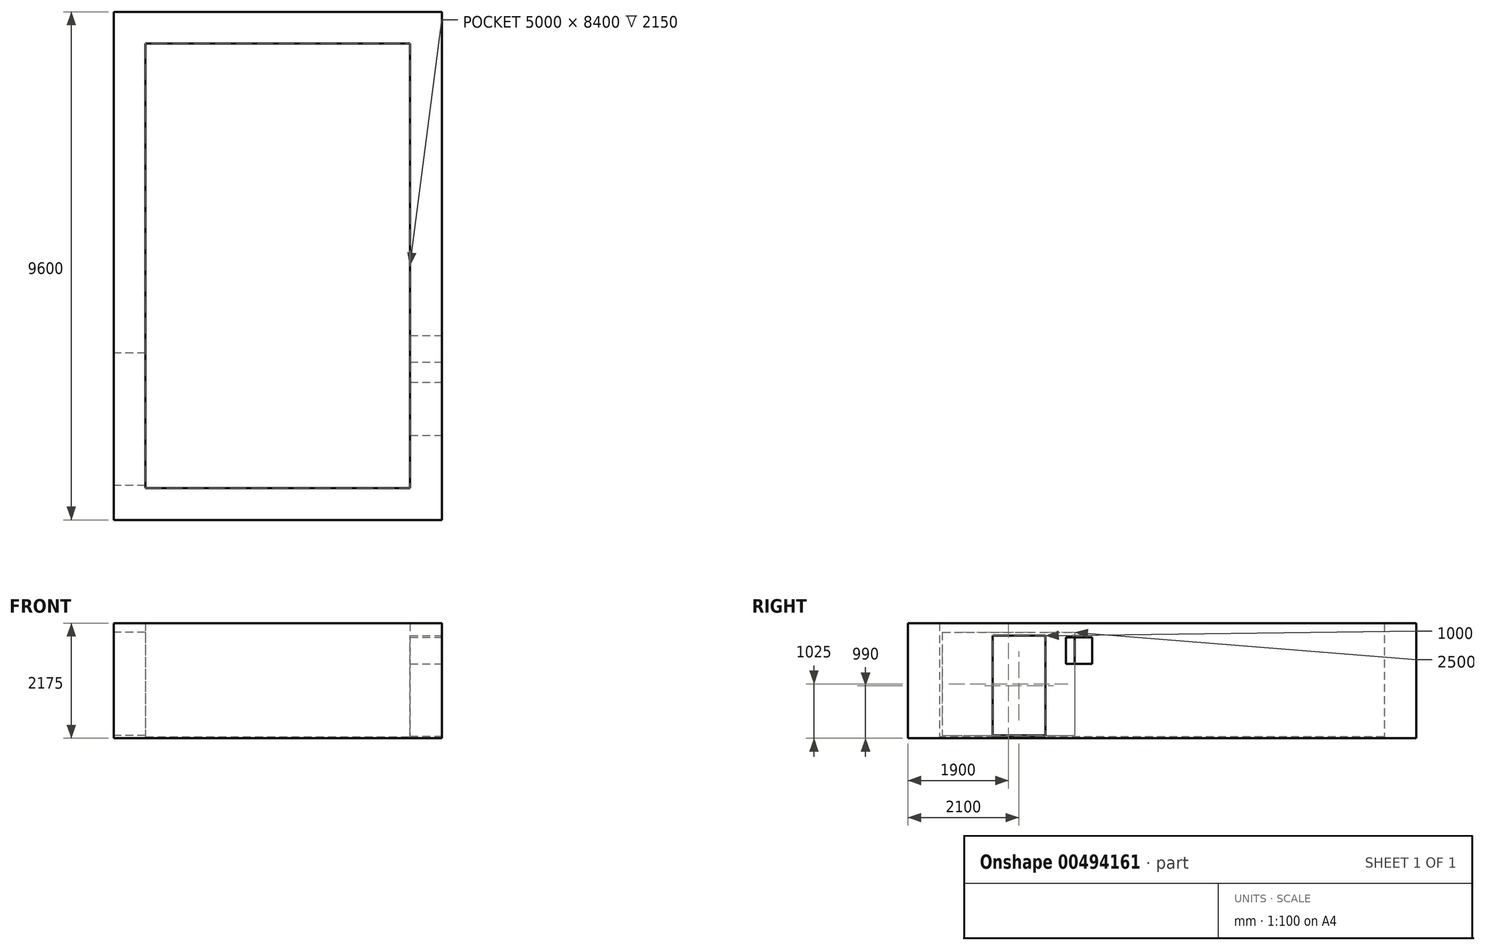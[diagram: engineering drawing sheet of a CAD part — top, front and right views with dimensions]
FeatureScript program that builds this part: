
annotation { "Feature Type Name" : "Feature", "Feature Type Description" : "" }
export const myFeature = defineFeature(function(context is Context, id is Id, definition is map)
    precondition{}
    {
        {
            var Q0;
            Q0=qCreatedBy(makeId("Top.planeOp"),FACE);
            var sketch = newSketch(context, id + "F0", { "sketchPlane" : qUnion([Q0])});
            skLineSegment(sketch, "E0.bottom", {"start": v(-2500, 4200) * mm, "end": v(2500, 4200) * mm});
            skLineSegment(sketch, "E0.top", {"start": v(-2500, -4200) * mm, "end": v(2500, -4200) * mm});
            skLineSegment(sketch, "E0.left", {"start": v(-2500, 4200) * mm, "end": v(-2500, -4200) * mm});
            skLineSegment(sketch, "E0.right", {"start": v(2500, 4200) * mm, "end": v(2500, -4200) * mm});
            skLineSegment(sketch, "E1", {"start": v(-2500, -4200) * mm, "end": v(2500, 4200) * mm, "construction": true});
            skLineSegment(sketch, "E2.0", {"start": v(3100, 4800) * mm, "end": v(3100, -4800) * mm});
            skLineSegment(sketch, "E2.1", {"start": v(-3100, 4800) * mm, "end": v(3100, 4800) * mm});
            skLineSegment(sketch, "E2.2", {"start": v(-3100, 4800) * mm, "end": v(-3100, -4800) * mm});
            skLineSegment(sketch, "E2.3", {"start": v(-3100, -4800) * mm, "end": v(3100, -4800) * mm});
            skSolve(sketch);
        }
        {
            var Q0;
            Q0 = qSketchRegion(id + "F0", true);
            extrude(context, id + "F1", {"entities" : qUnion([Q0]), "depth" : 2150 * mm, "offsetDistance" : 25 * mm});
        }
        {
            var Q0;
            Q0=makeQuery(id+"F1.opExtrude","CAP_FACE",FACE,{"disambiguationData":[OSD([sQuery(id+"F0.wireOp",EDGE,"E0.bottom"),sQuery(id+"F0.wireOp",EDGE,"E0.top"),sQuery(id+"F0.wireOp",EDGE,"E0.left"),sQuery(id+"F0.wireOp",EDGE,"E0.right"),sQuery(id+"F0.wireOp",EDGE,"E2.0"),sQuery(id+"F0.wireOp",EDGE,"E2.1"),sQuery(id+"F0.wireOp",EDGE,"E2.2"),sQuery(id+"F0.wireOp",EDGE,"E2.3")])],"isStart":true});
            var sketch = newSketch(context, id + "F2", { "sketchPlane" : qUnion([Q0])});
            skLineSegment(sketch, "E3.bottom", {"start": v(-3100, 4800) * mm, "end": v(3100, 4800) * mm});
            skLineSegment(sketch, "E3.top", {"start": v(-3100, -4800) * mm, "end": v(3100, -4800) * mm});
            skLineSegment(sketch, "E3.left", {"start": v(-3100, 4800) * mm, "end": v(-3100, -4800) * mm});
            skLineSegment(sketch, "E3.right", {"start": v(3100, 4800) * mm, "end": v(3100, -4800) * mm});
            skSolve(sketch);
        }
        {
            var Q0;
            Q0 = qSketchRegion(id + "F2", true);
            extrude(context, id + "F3", {"entities" : qUnion([Q0]), "operationType" : NewBodyOperationType.ADD, "depth" : 25 * mm, "offsetDistance" : 25 * mm});
        }
        {
            var Q0;
            Q0=makeQuery(id+"F3.boolean.opBoolean","MERGE",FACE,{"derivedFrom":[makeQuery(id+"F1.opExtrude","SWEPT_FACE",FACE,{"disambiguationData":[OSD([sQuery(id+"F0.wireOp",EDGE,"E2.2")])]}),makeQuery(id+"F3.opExtrude","SWEPT_FACE",FACE,{"disambiguationData":[OSD([sQuery(id+"F2.wireOp",EDGE,"E3.left")])]})]});
            var sketch = newSketch(context, id + "F4", { "sketchPlane" : qUnion([Q0])});
            skLineSegment(sketch, "E4.bottom", {"start": v(4150, 1975) * mm, "end": v(1650, 1975) * mm});
            skLineSegment(sketch, "E4.top", {"start": v(4150, 25) * mm, "end": v(1650, 25) * mm});
            skLineSegment(sketch, "E4.left", {"start": v(4150, 1975) * mm, "end": v(4150, 25) * mm});
            skLineSegment(sketch, "E4.right", {"start": v(1650, 1975) * mm, "end": v(1650, 25) * mm});
            skSolve(sketch);
        }
        {
            var Q0;
            Q0 = qSketchRegion(id + "F4", true);
            extrude(context, id + "F5", {"entities" : qUnion([Q0]), "operationType" : NewBodyOperationType.REMOVE, "endBound" : BoundingType.UP_TO_NEXT, "oppositeDirection" : true, "depth" : 25 * mm, "offsetDistance" : 25 * mm});
        }
        {
            var Q0;
            Q0=makeQuery(id+"F3.boolean.opBoolean","MERGE",FACE,{"derivedFrom":[makeQuery(id+"F1.opExtrude","SWEPT_FACE",FACE,{"disambiguationData":[OSD([sQuery(id+"F0.wireOp",EDGE,"E2.0")])]}),makeQuery(id+"F3.opExtrude","SWEPT_FACE",FACE,{"disambiguationData":[OSD([sQuery(id+"F2.wireOp",EDGE,"E3.right")])]})]});
            var sketch = newSketch(context, id + "F6", { "sketchPlane" : qUnion([Q0])});
            skLineSegment(sketch, "E5.bottom", {"start": v(-3200, 1915) * mm, "end": v(-2200, 1915) * mm});
            skLineSegment(sketch, "E5.top", {"start": v(-3200, 15) * mm, "end": v(-2200, 15) * mm});
            skLineSegment(sketch, "E5.left", {"start": v(-3200, 1915) * mm, "end": v(-3200, 15) * mm});
            skLineSegment(sketch, "E5.right", {"start": v(-2200, 1915) * mm, "end": v(-2200, 15) * mm});
            skLineSegment(sketch, "E6.bottom", {"start": v(-1816.2, 1880.92) * mm, "end": v(-1316.2, 1880.92) * mm});
            skLineSegment(sketch, "E6.top", {"start": v(-1816.2, 1380.92) * mm, "end": v(-1316.2, 1380.92) * mm});
            skLineSegment(sketch, "E6.left", {"start": v(-1816.2, 1880.92) * mm, "end": v(-1816.2, 1380.92) * mm});
            skLineSegment(sketch, "E6.right", {"start": v(-1316.2, 1880.92) * mm, "end": v(-1316.2, 1380.92) * mm});
            skSolve(sketch);
        }
        {
            var Q0;
            Q0 = qSketchRegion(id + "F6", true);
            extrude(context, id + "F7", {"entities" : qUnion([Q0]), "operationType" : NewBodyOperationType.REMOVE, "endBound" : BoundingType.UP_TO_NEXT, "oppositeDirection" : true, "depth" : 25 * mm, "offsetDistance" : 25 * mm});
        }
    });
